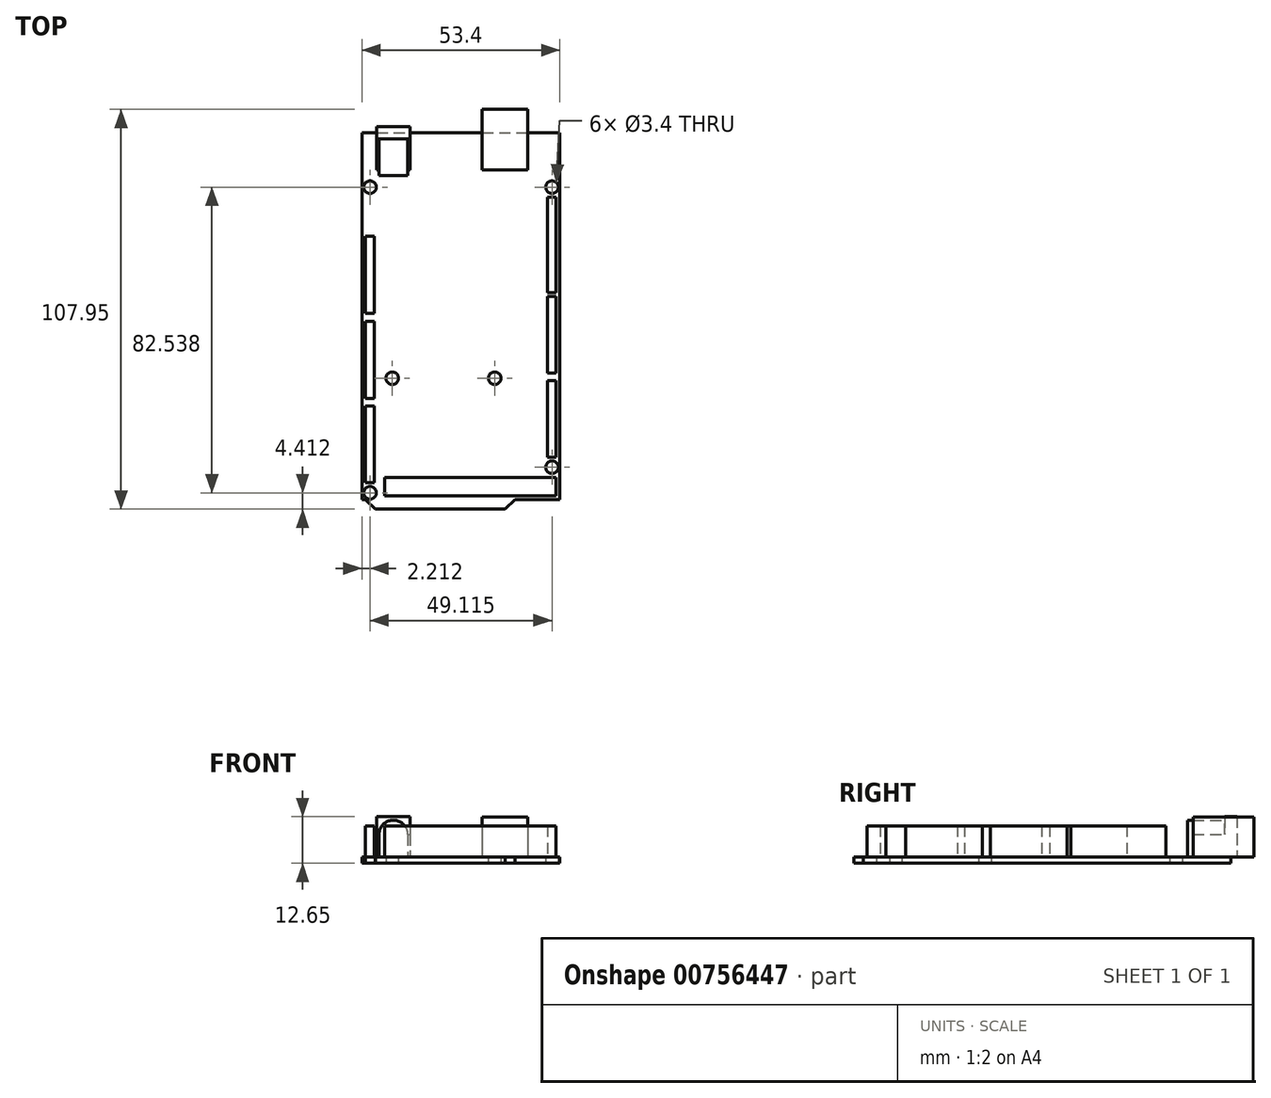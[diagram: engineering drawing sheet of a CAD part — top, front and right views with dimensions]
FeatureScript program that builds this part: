
annotation { "Feature Type Name" : "Feature", "Feature Type Description" : "" }
export const myFeature = defineFeature(function(context is Context, id is Id, definition is map)
    precondition{}
    {
        {
            var Q0;
            Q0=qCreatedBy(makeId("Top.planeOp"),FACE);
            var sketch = newSketch(context, id + "F0", { "sketchPlane" : qUnion([Q0])});
            skLineSegment(sketch, "E0.bottom", {"start": v(-23.1, -50.85) * mm, "end": v(12, -50.85) * mm});
            skLineSegment(sketch, "E0.top", {"start": v(-26.7, 50.85) * mm, "end": v(26.7, 50.85) * mm});
            skLineSegment(sketch, "E0.left", {"start": v(-26.7, -48.25) * mm, "end": v(-26.7, 50.85) * mm});
            skLineSegment(sketch, "E0.right", {"start": v(26.7, -48.25) * mm, "end": v(26.7, 50.85) * mm});
            skPoint(sketch, "E0.middle", {"position": v(0, 0) * mm});
            skLineSegment(sketch, "E1", {"start": v(-26.7, -48.25) * mm, "end": v(26.7, -48.25) * mm});
            skPoint(sketch, "E2", {"position": v(14.6, -48.25) * mm});
            skPoint(sketch, "E3", {"position": v(-25.7, -48.25) * mm});
            skLineSegment(sketch, "E4", {"start": v(-25.7, -48.25) * mm, "end": v(-23.1, -50.85) * mm});
            skLineSegment(sketch, "E5", {"start": v(14.6, -48.25) * mm, "end": v(12, -50.85) * mm});
            skPoint(sketch, "E6.orphan", {"position": v(-26.7, -50.85) * mm});
            skPoint(sketch, "E7.orphan", {"position": v(26.7, -50.85) * mm});
            skCircle(sketch, "E8", {"center": v(-24.49, -46.44) * mm, "radius": 1.7 * mm});
            skCircle(sketch, "E9", {"center": v(24.63, -39.53) * mm, "radius": 1.7 * mm});
            skLineSegment(sketch, "E10", {"start": v(26.7, -41.25) * mm, "end": v(21.7, -41.25) * mm, "construction": true});
            skCircle(sketch, "E11", {"center": v(-18.5, -15.5) * mm, "radius": 1.7 * mm});
            skCircle(sketch, "E12", {"center": v(9.15, -15.5) * mm, "radius": 1.7 * mm});
            skCircle(sketch, "E13", {"center": v(-24.49, 36.1) * mm, "radius": 1.7 * mm});
            skCircle(sketch, "E14", {"center": v(24.63, 36.1) * mm, "radius": 1.7 * mm});
            skSolve(sketch);
        }
        {
            var Q0;
            Q0=makeQuery(id+"F0.imprint","IMPRINT",FACE,{"disambiguationData":[TD([[makeQuery(id+"F0.imprint","IMPRINT",EDGE,{"derivedFrom":sQuery(id+"F0.wireOp",EDGE,"E0.top")}),-1.0]])]});
            var Q1;
            Q1=makeQuery(id+"F0.imprint","IMPRINT",FACE,{"disambiguationData":[TD([[makeQuery(id+"F0.imprint","IMPRINT",EDGE,{"derivedFrom":sQuery(id+"F0.wireOp",EDGE,"E0.bottom")}),1.0]])]});
            extrude(context, id + "F1", {"entities" : qUnion([Q0, Q1]), "depth" : 1.65 * mm, "offsetDistance" : 25 * mm});
        }
        {
            var Q0;
            Q0=makeQuery(id+"F1.opExtrude","CAP_FACE",FACE,{"disambiguationData":[OSD([sQuery(id+"F0.wireOp",EDGE,"E0.bottom"),sQuery(id+"F0.wireOp",EDGE,"E0.top"),sQuery(id+"F0.wireOp",EDGE,"E0.left"),sQuery(id+"F0.wireOp",EDGE,"E0.right"),sQuery(id+"F0.wireOp",EDGE,"E1"),sQuery(id+"F0.wireOp",EDGE,"E4"),sQuery(id+"F0.wireOp",EDGE,"E5"),sQuery(id+"F0.wireOp",EDGE,"E8"),sQuery(id+"F0.wireOp",EDGE,"E9"),sQuery(id+"F0.wireOp",EDGE,"E11"),sQuery(id+"F0.wireOp",EDGE,"E12"),sQuery(id+"F0.wireOp",EDGE,"E13"),sQuery(id+"F0.wireOp",EDGE,"E14")])],"isStart":false});
            var sketch = newSketch(context, id + "F2", { "sketchPlane" : qUnion([Q0])});
            skLineSegment(sketch, "E15.0", {"start": v(-26.7, 50.85) * mm, "end": v(26.7, 50.85) * mm, "construction": true});
            skLineSegment(sketch, "E16.bottom", {"start": v(-22.7, 49.2) * mm, "end": v(-13.7, 49.2) * mm});
            skLineSegment(sketch, "E16.top", {"start": v(-22.7, 52.5) * mm, "end": v(-13.7, 52.5) * mm});
            skLineSegment(sketch, "E16.left", {"start": v(-22.7, 49.2) * mm, "end": v(-22.7, 52.5) * mm});
            skLineSegment(sketch, "E16.right", {"start": v(-13.7, 49.2) * mm, "end": v(-13.7, 52.5) * mm});
            skPoint(sketch, "E16.middle", {"position": v(-18.2, 50.85) * mm});
            skSolve(sketch);
        }
        {
            var Q0;
            {var subQ0=sQuery(id+"F2.wireOp",EDGE,"E16.bottom");Q0=makeQuery(id+"F2.imprint","IMPRINT",FACE,{"disambiguationData":[TD([[makeQuery(id+"F2.imprint","IMPRINT",EDGE,{"derivedFrom":subQ0}),1.0]])]});}
            var Q1;
            {var subQ0=sQuery(id+"F2.wireOp",EDGE,"E16.top");Q1=makeQuery(id+"F2.imprint","IMPRINT",FACE,{"disambiguationData":[TD([[makeQuery(id+"F2.imprint","IMPRINT",EDGE,{"derivedFrom":subQ0}),-1.0]])]});}
            extrude(context, id + "F3", {"entities" : qUnion([Q0, Q1]), "depth" : 11 * mm, "offsetDistance" : 25 * mm});
        }
        {
            var Q0;
            Q0=makeQuery(id+"F3.opExtrude","SWEPT_FACE",FACE,{"disambiguationData":[OSD([sQuery(id+"F2.wireOp",EDGE,"E16.bottom")])]});
            var sketch = newSketch(context, id + "F4", { "sketchPlane" : qUnion([Q0])});
            skArc(sketch, "E17", {"start": v(-14.3, 7.75) * mm, "mid": v(-18.2, 11.65) * mm, "end": v(-22.1, 7.75) * mm});
            skPoint(sketch, "E17.centerSnap0", {"position": v(-18.2, 12.65) * mm});
            skLineSegment(sketch, "E18", {"start": v(-22.1, 7.75) * mm, "end": v(-22.1, 1.65) * mm});
            skLineSegment(sketch, "E19", {"start": v(-14.3, 7.75) * mm, "end": v(-14.3, 1.65) * mm});
            skPoint(sketch, "E19.endSnap0", {"position": v(-18.2, 1.65) * mm});
            skLineSegment(sketch, "E20.0", {"start": v(-22.7, 1.65) * mm, "end": v(-13.7, 1.65) * mm});
            skSolve(sketch);
        }
        {
            var Q0;
            Q0=makeQuery(id+"F4.imprint","IMPRINT",FACE,{"disambiguationData":[TD([[makeQuery(id+"F4.imprint","IMPRINT",EDGE,{"derivedFrom":sQuery(id+"F4.wireOp",EDGE,"E17")}),1.0]])]});
            extrude(context, id + "F5", {"entities" : qUnion([Q0]), "operationType" : NewBodyOperationType.ADD, "depth" : 10 * mm, "offsetDistance" : 25 * mm});
        }
        {
            var Q0;
            Q0=makeQuery(id+"F3.opExtrude","SWEPT_FACE",FACE,{"disambiguationData":[OSD([sQuery(id+"F2.wireOp",EDGE,"E16.bottom")])]});
            var sketch = newSketch(context, id + "F6", { "sketchPlane" : qUnion([Q0])});
            skLineSegment(sketch, "E21.0", {"start": v(-14.3, 7.75) * mm, "end": v(-14.3, 1.65) * mm});
            skLineSegment(sketch, "E21.1", {"start": v(-13.7, 12.65) * mm, "end": v(-13.7, 1.65) * mm});
            skLineSegment(sketch, "E21.2", {"start": v(-22.1, 7.75) * mm, "end": v(-22.1, 1.65) * mm});
            skLineSegment(sketch, "E21.3", {"start": v(-22.7, 12.65) * mm, "end": v(-22.7, 1.65) * mm});
            skLineSegment(sketch, "E22", {"start": v(-22.1, 7.75) * mm, "end": v(-22.7, 7.75) * mm});
            skLineSegment(sketch, "E23", {"start": v(-14.3, 7.75) * mm, "end": v(-13.7, 7.75) * mm});
            skSolve(sketch);
        }
        {
            var Q0;
            Q0=makeQuery(id+"F6.imprint","IMPRINT",FACE,{"disambiguationData":[TD([[makeQuery(id+"F6.imprint","IMPRINT",EDGE,{"derivedFrom":sQuery(id+"F6.wireOp",EDGE,"E21.2")}),-1.0]])]});
            var Q1;
            Q1=makeQuery(id+"F6.imprint","IMPRINT",FACE,{"disambiguationData":[TD([[makeQuery(id+"F6.imprint","IMPRINT",EDGE,{"derivedFrom":sQuery(id+"F6.wireOp",EDGE,"E21.0")}),1.0]])]});
            extrude(context, id + "F7", {"entities" : qUnion([Q0, Q1]), "operationType" : NewBodyOperationType.ADD, "depth" : 8.5 * mm, "offsetDistance" : 25 * mm});
        }
        {
            var Q0;
            Q0=makeQuery(id+"F1.opExtrude","CAP_FACE",FACE,{"disambiguationData":[OSD([sQuery(id+"F0.wireOp",EDGE,"E0.bottom"),sQuery(id+"F0.wireOp",EDGE,"E0.top"),sQuery(id+"F0.wireOp",EDGE,"E0.left"),sQuery(id+"F0.wireOp",EDGE,"E0.right"),sQuery(id+"F0.wireOp",EDGE,"E1"),sQuery(id+"F0.wireOp",EDGE,"E4"),sQuery(id+"F0.wireOp",EDGE,"E5"),sQuery(id+"F0.wireOp",EDGE,"E8"),sQuery(id+"F0.wireOp",EDGE,"E9"),sQuery(id+"F0.wireOp",EDGE,"E11"),sQuery(id+"F0.wireOp",EDGE,"E12"),sQuery(id+"F0.wireOp",EDGE,"E13"),sQuery(id+"F0.wireOp",EDGE,"E14")])],"isStart":false});
            var sketch = newSketch(context, id + "F8", { "sketchPlane" : qUnion([Q0])});
            skPoint(sketch, "E24.0", {"position": v(-13.7, 40.7) * mm});
            skLineSegment(sketch, "E25.bottom", {"start": v(5.8, 40.7) * mm, "end": v(18.1, 40.7) * mm});
            skLineSegment(sketch, "E25.top", {"start": v(5.8, 57.1) * mm, "end": v(18.1, 57.1) * mm});
            skLineSegment(sketch, "E25.left", {"start": v(5.8, 40.7) * mm, "end": v(5.8, 57.1) * mm});
            skLineSegment(sketch, "E25.right", {"start": v(18.1, 40.7) * mm, "end": v(18.1, 57.1) * mm});
            skSolve(sketch);
        }
        {
            var Q0;
            {var subQ0=sQuery(id+"F8.wireOp",EDGE,"E25.bottom");Q0=makeQuery(id+"F8.imprint","IMPRINT",FACE,{"disambiguationData":[TD([[makeQuery(id+"F8.imprint","IMPRINT",EDGE,{"derivedFrom":subQ0}),1.0]])]});}
            var Q1;
            {var subQ0=sQuery(id+"F8.wireOp",EDGE,"E25.top");Q1=makeQuery(id+"F8.imprint","IMPRINT",FACE,{"disambiguationData":[TD([[makeQuery(id+"F8.imprint","IMPRINT",EDGE,{"derivedFrom":subQ0}),-1.0]])]});}
            extrude(context, id + "F9", {"entities" : qUnion([Q0, Q1]), "depth" : 10.9 * mm, "offsetDistance" : 25 * mm});
        }
        {
            var Q0;
            Q0=makeQuery(id+"F1.opExtrude","CAP_FACE",FACE,{"disambiguationData":[OSD([sQuery(id+"F0.wireOp",EDGE,"E0.bottom"),sQuery(id+"F0.wireOp",EDGE,"E0.top"),sQuery(id+"F0.wireOp",EDGE,"E0.left"),sQuery(id+"F0.wireOp",EDGE,"E0.right"),sQuery(id+"F0.wireOp",EDGE,"E1"),sQuery(id+"F0.wireOp",EDGE,"E4"),sQuery(id+"F0.wireOp",EDGE,"E5"),sQuery(id+"F0.wireOp",EDGE,"E8"),sQuery(id+"F0.wireOp",EDGE,"E9"),sQuery(id+"F0.wireOp",EDGE,"E11"),sQuery(id+"F0.wireOp",EDGE,"E12"),sQuery(id+"F0.wireOp",EDGE,"E13"),sQuery(id+"F0.wireOp",EDGE,"E14")])],"isStart":false});
            var sketch = newSketch(context, id + "F10", { "sketchPlane" : qUnion([Q0])});
            skLineSegment(sketch, "E26.bottom", {"start": v(25.7, 33.4) * mm, "end": v(23.35, 33.4) * mm});
            skLineSegment(sketch, "E26.top", {"start": v(25.7, 7.65) * mm, "end": v(23.35, 7.65) * mm});
            skLineSegment(sketch, "E26.left", {"start": v(25.7, 33.4) * mm, "end": v(25.7, 7.65) * mm});
            skLineSegment(sketch, "E26.right", {"start": v(23.35, 33.4) * mm, "end": v(23.35, 7.65) * mm});
            skLineSegment(sketch, "E27.bottom", {"start": v(23.35, 6.65) * mm, "end": v(25.7, 6.65) * mm});
            skLineSegment(sketch, "E27.top", {"start": v(23.35, -14.05) * mm, "end": v(25.7, -14.05) * mm});
            skLineSegment(sketch, "E27.left", {"start": v(23.35, 6.65) * mm, "end": v(23.35, -14.05) * mm});
            skLineSegment(sketch, "E27.right", {"start": v(25.7, 6.65) * mm, "end": v(25.7, -14.05) * mm});
            skLineSegment(sketch, "E28.bottom", {"start": v(23.35, -16.13) * mm, "end": v(25.7, -16.13) * mm});
            skLineSegment(sketch, "E28.top", {"start": v(23.35, -36.83) * mm, "end": v(25.7, -36.83) * mm});
            skLineSegment(sketch, "E28.left", {"start": v(23.35, -16.13) * mm, "end": v(23.35, -36.83) * mm});
            skLineSegment(sketch, "E28.right", {"start": v(25.7, -16.13) * mm, "end": v(25.7, -36.83) * mm});
            skLineSegment(sketch, "E29.bottom", {"start": v(25.7, -42.25) * mm, "end": v(-20.5, -42.25) * mm});
            skLineSegment(sketch, "E29.top", {"start": v(25.7, -47.25) * mm, "end": v(-20.5, -47.25) * mm});
            skLineSegment(sketch, "E29.left", {"start": v(25.7, -42.25) * mm, "end": v(25.7, -47.25) * mm});
            skLineSegment(sketch, "E29.right", {"start": v(-20.5, -42.25) * mm, "end": v(-20.5, -47.25) * mm});
            skLineSegment(sketch, "E30.bottom", {"start": v(-23.35, -43.74) * mm, "end": v(-25.7, -43.74) * mm});
            skLineSegment(sketch, "E30.top", {"start": v(-23.35, -22.94) * mm, "end": v(-25.7, -22.94) * mm});
            skLineSegment(sketch, "E30.left", {"start": v(-23.35, -43.74) * mm, "end": v(-23.35, -22.94) * mm});
            skLineSegment(sketch, "E30.right", {"start": v(-25.7, -43.74) * mm, "end": v(-25.7, -22.94) * mm});
            skLineSegment(sketch, "E31.bottom", {"start": v(-23.35, -20.94) * mm, "end": v(-25.7, -20.94) * mm});
            skLineSegment(sketch, "E31.top", {"start": v(-23.35, -0.14) * mm, "end": v(-25.7, -0.14) * mm});
            skLineSegment(sketch, "E31.left", {"start": v(-23.35, -20.94) * mm, "end": v(-23.35, -0.14) * mm});
            skLineSegment(sketch, "E31.right", {"start": v(-25.7, -20.94) * mm, "end": v(-25.7, -0.14) * mm});
            skLineSegment(sketch, "E32.bottom", {"start": v(-23.35, 2.01) * mm, "end": v(-25.7, 2.01) * mm});
            skLineSegment(sketch, "E32.top", {"start": v(-23.35, 22.81) * mm, "end": v(-25.7, 22.81) * mm});
            skLineSegment(sketch, "E32.left", {"start": v(-23.35, 2.01) * mm, "end": v(-23.35, 22.81) * mm});
            skLineSegment(sketch, "E32.right", {"start": v(-25.7, 2.01) * mm, "end": v(-25.7, 22.81) * mm});
            skSolve(sketch);
        }
        {
            var Q0;
            Q0=makeQuery(id+"F10.imprint","IMPRINT",FACE,{"disambiguationData":[TD([[makeQuery(id+"F10.imprint","IMPRINT",EDGE,{"derivedFrom":sQuery(id+"F10.wireOp",EDGE,"E26.bottom")}),1.0]])]});
            var Q1;
            Q1=makeQuery(id+"F10.imprint","IMPRINT",FACE,{"disambiguationData":[TD([[makeQuery(id+"F10.imprint","IMPRINT",EDGE,{"derivedFrom":sQuery(id+"F10.wireOp",EDGE,"E27.bottom")}),-1.0]])]});
            var Q2;
            Q2=makeQuery(id+"F10.imprint","IMPRINT",FACE,{"disambiguationData":[TD([[makeQuery(id+"F10.imprint","IMPRINT",EDGE,{"derivedFrom":sQuery(id+"F10.wireOp",EDGE,"E28.bottom")}),-1.0]])]});
            var Q3;
            Q3=makeQuery(id+"F10.imprint","IMPRINT",FACE,{"disambiguationData":[TD([[makeQuery(id+"F10.imprint","IMPRINT",EDGE,{"derivedFrom":sQuery(id+"F10.wireOp",EDGE,"E29.bottom")}),1.0]])]});
            var Q4;
            Q4=makeQuery(id+"F10.imprint","IMPRINT",FACE,{"disambiguationData":[TD([[makeQuery(id+"F10.imprint","IMPRINT",EDGE,{"derivedFrom":sQuery(id+"F10.wireOp",EDGE,"E30.bottom")}),-1.0]])]});
            var Q5;
            Q5=makeQuery(id+"F10.imprint","IMPRINT",FACE,{"disambiguationData":[TD([[makeQuery(id+"F10.imprint","IMPRINT",EDGE,{"derivedFrom":sQuery(id+"F10.wireOp",EDGE,"E31.bottom")}),-1.0]])]});
            var Q6;
            Q6=makeQuery(id+"F10.imprint","IMPRINT",FACE,{"disambiguationData":[TD([[makeQuery(id+"F10.imprint","IMPRINT",EDGE,{"derivedFrom":sQuery(id+"F10.wireOp",EDGE,"E32.bottom")}),-1.0]])]});
            extrude(context, id + "F11", {"entities" : qUnion([Q0, Q1, Q2, Q3, Q4, Q5, Q6]), "depth" : 8.5 * mm, "offsetDistance" : 25 * mm});
        }
    });
